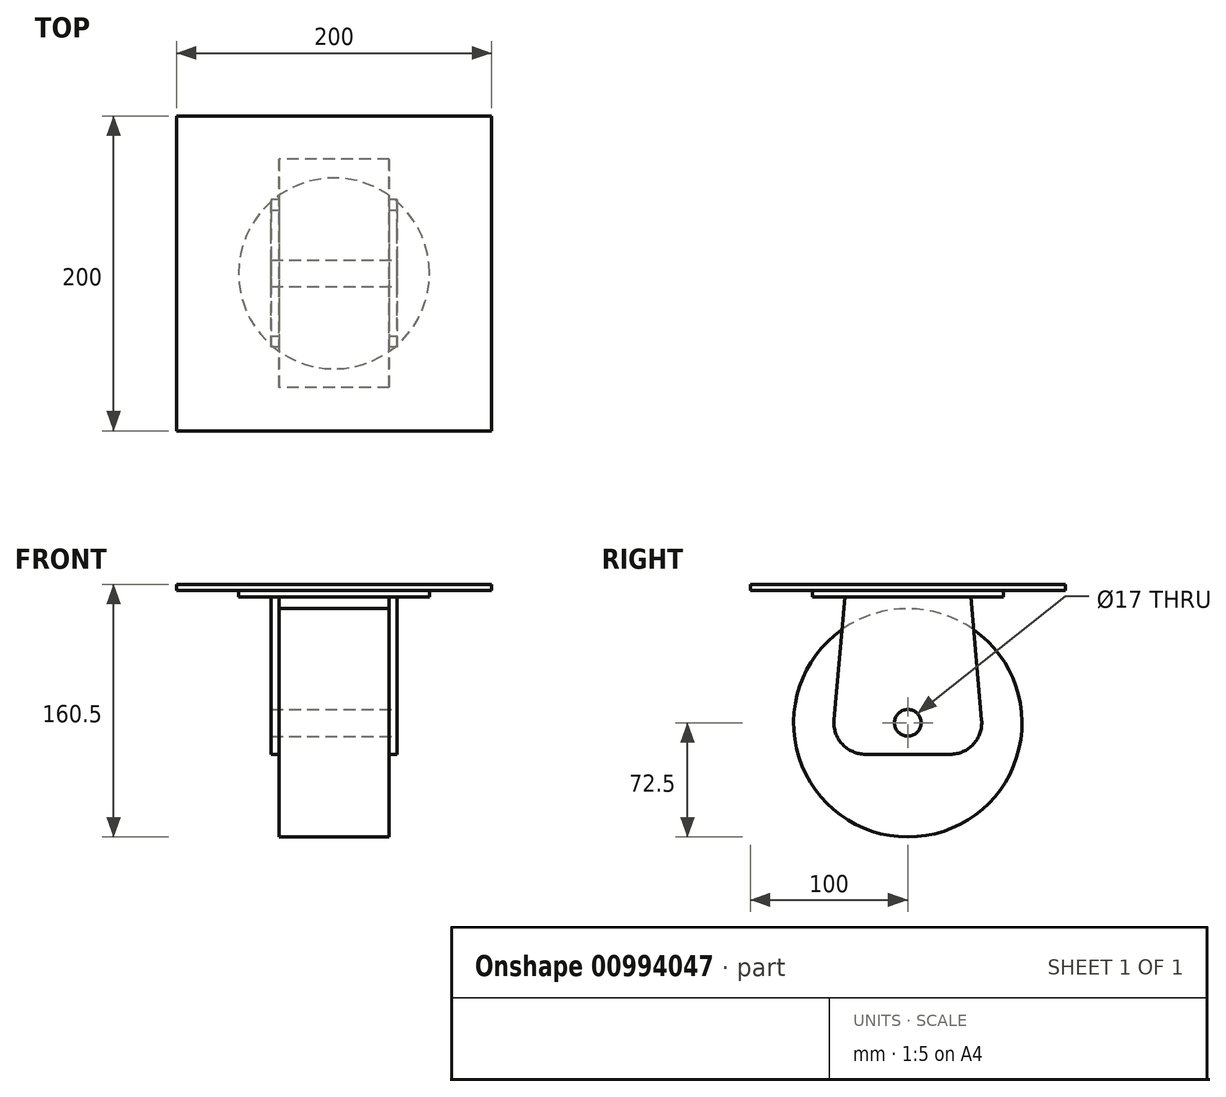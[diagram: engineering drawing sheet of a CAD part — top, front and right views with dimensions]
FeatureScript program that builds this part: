
annotation { "Feature Type Name" : "Feature", "Feature Type Description" : "" }
export const myFeature = defineFeature(function(context is Context, id is Id, definition is map)
    precondition{}
    {
        {
            var Q0;
            Q0=qCreatedBy(makeId("Top.planeOp"),FACE);
            var sketch = newSketch(context, id + "F0", { "sketchPlane" : qUnion([Q0])});
            skLineSegment(sketch, "E0.bottom", {"start": v(100, 100) * mm, "end": v(-100, 100) * mm});
            skLineSegment(sketch, "E0.top", {"start": v(100, -100) * mm, "end": v(-100, -100) * mm});
            skLineSegment(sketch, "E0.left", {"start": v(100, 100) * mm, "end": v(100, -100) * mm});
            skLineSegment(sketch, "E0.right", {"start": v(-100, 100) * mm, "end": v(-100, -100) * mm});
            skPoint(sketch, "E0.middle", {"position": v(0, 0) * mm});
            skSolve(sketch);
        }
        {
            var Q0;
            Q0=makeQuery(id+"F0.imprint","IMPRINT",FACE,{"disambiguationData":[TD([[makeQuery(id+"F0.imprint","IMPRINT",EDGE,{"derivedFrom":sQuery(id+"F0.wireOp",EDGE,"E0.bottom")}),1.0]])]});
            extrude(context, id + "F1", {"entities" : qUnion([Q0]), "oppositeDirection" : true, "depth" : 4 * mm, "offsetDistance" : 25 * mm});
        }
        {
            var Q0;
            Q0=makeQuery(id+"F1.opExtrude","CAP_FACE",FACE,{"disambiguationData":[OSD([sQuery(id+"F0.wireOp",EDGE,"E0.bottom"),sQuery(id+"F0.wireOp",EDGE,"E0.top"),sQuery(id+"F0.wireOp",EDGE,"E0.left"),sQuery(id+"F0.wireOp",EDGE,"E0.right")])],"isStart":false});
            var sketch = newSketch(context, id + "F2", { "sketchPlane" : qUnion([Q0])});
            skCircle(sketch, "E1", {"center": v(0, 0) * mm, "radius": 60.62 * mm});
            skSolve(sketch);
        }
        {
            var Q0;
            Q0=makeQuery(id+"F2.imprint","IMPRINT",FACE,{"disambiguationData":[TD([[makeQuery(id+"F2.imprint","IMPRINT",EDGE,{"derivedFrom":sQuery(id+"F2.wireOp",EDGE,"E1")}),1.0]])]});
            extrude(context, id + "F3", {"entities" : qUnion([Q0]), "operationType" : NewBodyOperationType.ADD, "depth" : 4 * mm, "offsetDistance" : 25 * mm});
        }
        {
            var Q0;
            Q0=qCreatedBy(makeId("Right.planeOp"),FACE);
            var sketch = newSketch(context, id + "F4", { "sketchPlane" : qUnion([Q0])});
            skLineSegment(sketch, "E2", {"start": v(-40, -8) * mm, "end": v(-46.85, -86.26) * mm});
            skLineSegment(sketch, "E3", {"start": v(-26.92, -108) * mm, "end": v(26.92, -108) * mm});
            skLineSegment(sketch, "E4", {"start": v(46.85, -86.26) * mm, "end": v(40, -8) * mm});
            skLineSegment(sketch, "E5.0", {"start": v(60.62, -8) * mm, "end": v(-60.62, -8) * mm});
            skLineSegment(sketch, "E6", {"start": v(-40, -8) * mm, "end": v(40, -8) * mm});
            skLineSegment(sketch, "E7", {"start": v(0, 38.66) * mm, "end": v(0, -161.65) * mm, "construction": true});
            skPoint(sketch, "E8.visualSharp", {"position": v(-48.75, -108) * mm});
            skArc(sketch, "E8.filletArc", {"start": v(-46.85, -86.26) * mm, "mid": v(-41.67, -101.51) * mm, "end": v(-26.92, -108) * mm});
            skPoint(sketch, "E9.visualSharp", {"position": v(48.75, -108) * mm});
            skArc(sketch, "E9.filletArc", {"start": v(26.92, -108) * mm, "mid": v(41.67, -101.51) * mm, "end": v(46.85, -86.26) * mm});
            skSolve(sketch);
        }
        {
            var Q0;
            Q0=makeQuery(id+"F4.imprint","IMPRINT",FACE,{"disambiguationData":[TD([[makeQuery(id+"F4.imprint","IMPRINT",EDGE,{"derivedFrom":sQuery(id+"F4.wireOp",EDGE,"E2")}),1.0]])]});
            extrude(context, id + "F5", {"entities" : qUnion([Q0]), "operationType" : NewBodyOperationType.ADD, "endBound" : BoundingType.SYMMETRIC, "depth" : 80 * mm, "offsetDistance" : 25 * mm});
        }
        {
            var Q0;
            Q0=qCreatedBy(makeId("Front.planeOp"),FACE);
            var sketch = newSketch(context, id + "F6", { "sketchPlane" : qUnion([Q0])});
            skLineSegment(sketch, "E10.0", {"start": v(35, -8) * mm, "end": v(-35, -8) * mm});
            skLineSegment(sketch, "E11.0", {"start": v(35, -108) * mm, "end": v(-35, -108) * mm});
            skLineSegment(sketch, "E12", {"start": v(-35, -8) * mm, "end": v(-35, -108) * mm});
            skLineSegment(sketch, "E13", {"start": v(35, -8) * mm, "end": v(35, -108) * mm});
            skPoint(sketch, "E14.orphan", {"position": v(-60.62, -8) * mm});
            skPoint(sketch, "E15.orphan", {"position": v(60.62, -8) * mm});
            skPoint(sketch, "E16.orphan", {"position": v(-40, -108) * mm});
            skPoint(sketch, "E17.orphan", {"position": v(40, -108) * mm});
            skSolve(sketch);
        }
        {
            var Q0;
            Q0 = qSketchRegion(id + "F6", true);
            extrude(context, id + "F7", {"entities" : qUnion([Q0]), "operationType" : NewBodyOperationType.REMOVE, "endBound" : BoundingType.UP_TO_NEXT, "oppositeDirection" : true, "depth" : 25 * mm, "offsetDistance" : 25 * mm, "hasSecondDirection" : true, "secondDirectionBound" : SecondDirectionBoundingType.UP_TO_NEXT, "secondDirectionOppositeDirection" : false, "secondDirectionDepth" : 25 * mm});
        }
        {
            var Q0;
            Q0=qCreatedBy(makeId("Right.planeOp"),FACE);
            var sketch = newSketch(context, id + "F8", { "sketchPlane" : qUnion([Q0])});
            skCircle(sketch, "E18", {"center": v(0, -88) * mm, "radius": 8.5 * mm});
            skSolve(sketch);
        }
        {
            var Q0;
            Q0 = qSketchRegion(id + "F8", true);
            var Q1;
            Q1=makeQuery(id+"F5.opExtrude","CAP_FACE",FACE,{"disambiguationData":[OSD([sQuery(id+"F4.wireOp",EDGE,"E2"),sQuery(id+"F4.wireOp",EDGE,"E3"),sQuery(id+"F4.wireOp",EDGE,"E4"),sQuery(id+"F4.wireOp",EDGE,"E6"),sQuery(id+"F4.wireOp",EDGE,"E8.filletArc"),sQuery(id+"F4.wireOp",EDGE,"E9.filletArc")])],"isStart":true});
            var Q2;
            Q2=makeQuery(id+"F5.opExtrude","CAP_FACE",FACE,{"disambiguationData":[OSD([sQuery(id+"F4.wireOp",EDGE,"E2"),sQuery(id+"F4.wireOp",EDGE,"E3"),sQuery(id+"F4.wireOp",EDGE,"E4"),sQuery(id+"F4.wireOp",EDGE,"E6"),sQuery(id+"F4.wireOp",EDGE,"E8.filletArc"),sQuery(id+"F4.wireOp",EDGE,"E9.filletArc")])],"isStart":false});
            extrude(context, id + "F9", {"entities" : qUnion([Q0]), "operationType" : NewBodyOperationType.REMOVE, "endBound" : BoundingType.UP_TO_SURFACE, "oppositeDirection" : true, "depth" : 25 * mm, "endBoundEntityFace" : qUnion([Q1]), "offsetDistance" : 25 * mm, "hasSecondDirection" : true, "secondDirectionBound" : SecondDirectionBoundingType.UP_TO_SURFACE, "secondDirectionOppositeDirection" : false, "secondDirectionDepth" : 25 * mm, "secondDirectionBoundEntityFace" : qUnion([Q2])});
        }
        {
            var Q0;
            Q0=qCreatedBy(makeId("Right.planeOp"),FACE);
            var sketch = newSketch(context, id + "F10", { "sketchPlane" : qUnion([Q0])});
            skCircle(sketch, "E19.0", {"center": v(0, -88) * mm, "radius": 8.5 * mm});
            skCircle(sketch, "E20", {"center": v(0, -88) * mm, "radius": 72.5 * mm});
            skSolve(sketch);
        }
        {
            var Q0;
            Q0=makeQuery(id+"F10.imprint","IMPRINT",FACE,{"disambiguationData":[TD([[makeQuery(id+"F10.imprint","IMPRINT",EDGE,{"derivedFrom":sQuery(id+"F10.wireOp",EDGE,"E19.0")}),-1.0]])]});
            extrude(context, id + "F11", {"entities" : qUnion([Q0]), "operationType" : NewBodyOperationType.ADD, "endBound" : BoundingType.SYMMETRIC, "depth" : 70 * mm, "offsetDistance" : 25 * mm});
        }
    });
